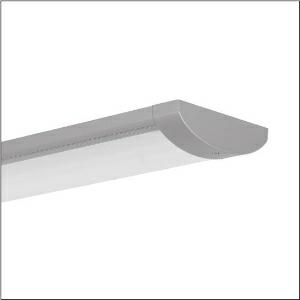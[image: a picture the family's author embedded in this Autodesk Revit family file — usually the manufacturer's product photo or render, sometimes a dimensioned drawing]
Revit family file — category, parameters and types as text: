
# Revit family: tv_20_5xa86174n0j
name_source: partatom
category: Lighting Fixtures
units: mm (PartAtom-declared; Revit-internal decimal feet)

## family parameters
Cut with Voids When Loaded = No
Host = Face
Light Source = No
Part Type = Normal
Room Calculation Point = No
Round Connector Dimension = Use Diameter
Shared = No

## types (1)
- TV 20 (1 x LED 4000K / CRI = 80 (unbekannt), 3960 lm, 4000K)
    Apparent Load = 37 VA
    CIE Flux Codes = 48 78 95 99 100
    Color Rendering = 80
    Color Temperature = 4000K
    Default Elevation = 1800 mm
    Description = TV 20, vandal-proof luminaire, primary light control with specular reflector, of aluminium, matt, primary optical cover: enclosure, of PC, frosted, light emission: direct distribution, primary light characteristic: symmetric, installation type: surface-mounted, LED, rated luminous flux: 3.960lm, luminous efficacy: 107lm/W, light colour: 840, colour temperature: 4000K, control gear: ON/OFF, mains connection: 230V, AC, 50Hz, rated input power: 37W, luminaire housing, of aluminium, coated, Siteco® metallic grey (DB 702S), with wall and ceiling fixing element, length: 1.261mm, width: 260mm, height: 70mm, mounting height: 2.5..4.0m, protection rating (complete): IP65, insulation class (complete): insulation class I (protective earthing), certification: CE, protection symbol: F, impact resistance: 2x IK10, standard: EN 60598, packaging unit: 1 piece
    Height = 70 mm
    Lamp = 1 x LED 4000K / CRI >= 80 (unbekannt)
    Lamp Light Flux = 3960 lm
    Lamp count = 1
    Length = 1261 mm
    Luminous efficacy = 107 lm/W
    Manufacturer = Siteco
    ModVariant = No
    Model = 5XA86174N0J
    Mounting Place = Ceiling
    Mounting Type = Surface mounted
    Number of Poles = 1
    OnlyDefault = Yes
    Power Factor = 1
    Product Name = TV 20
    Product group = vandal-proof luminaire
    ProductGroupID = 309
    Protection Class = Protection class I
    Protection Degree = IP 65
    RLX_Detail_Level = 1
    RLX_Emergency_Light_Flux = 0 lm
    RLX_Emergency_Type = 0
    RLX_Emergency_Type_DB = No
    RlxData = <blob elided: 25669 chars, md5=07f52a11>
    Socket = socket
    Standby Power = 0 W
    System Light Flux = 3960 lm
    System Power = 37 W
    Type Comments = Product without accessories
    Type Image = l_1004809.jpg
    URL = http://relux.com
    VarID = ---
    Voltage = 0 V
    Weight = 0.00 kg
    Width = 260 mm

## geometry (parser evidence)
native form markers: Blend x4, Sweep x10
no freeform markers — native parametric forms only
